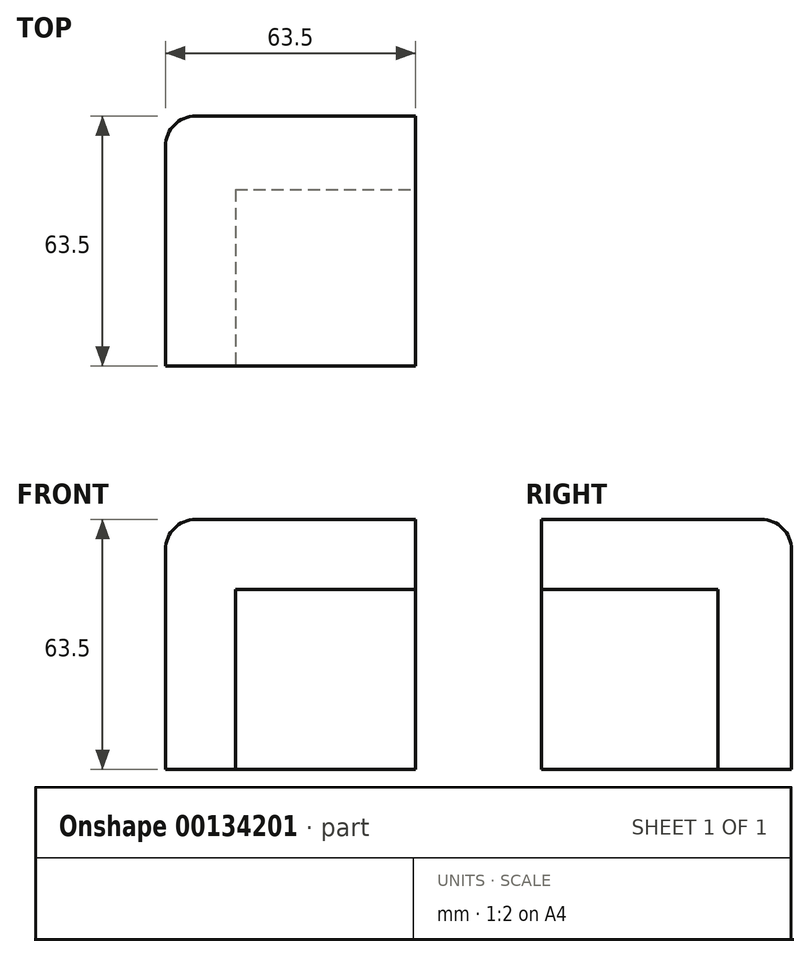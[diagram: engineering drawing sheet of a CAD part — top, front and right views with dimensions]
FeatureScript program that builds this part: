
annotation { "Feature Type Name" : "Feature", "Feature Type Description" : "" }
export const myFeature = defineFeature(function(context is Context, id is Id, definition is map)
    precondition{}
    {
        {
            var Q0;
            Q0=qCreatedBy(makeId("Front.planeOp"),FACE);
            var sketch = newSketch(context, id + "F0", { "sketchPlane" : qUnion([Q0])});
            skLineSegment(sketch, "E0.bottom", {"start": v(-31.75, 31.75) * mm, "end": v(31.75, 31.75) * mm});
            skLineSegment(sketch, "E0.top", {"start": v(-31.75, -31.75) * mm, "end": v(31.75, -31.75) * mm});
            skLineSegment(sketch, "E0.left", {"start": v(-31.75, 31.75) * mm, "end": v(-31.75, -31.75) * mm});
            skLineSegment(sketch, "E0.right", {"start": v(31.75, 31.75) * mm, "end": v(31.75, -31.75) * mm});
            skPoint(sketch, "E0.middle", {"position": v(0, 0) * mm});
            skSolve(sketch);
        }
        {
            var Q0;
            Q0=makeQuery(id+"F0.imprint","IMPRINT",FACE,{"disambiguationData":[TD([[makeQuery(id+"F0.imprint","IMPRINT",EDGE,{"derivedFrom":sQuery(id+"F0.wireOp",EDGE,"E0.bottom")}),-1.0]])]});
            extrude(context, id + "F1", {"entities" : qUnion([Q0]), "depth" : 63.5 * mm});
        }
        {
            var Q0;
            Q0=makeQuery(id+"F1.opExtrude","CAP_FACE",FACE,{"disambiguationData":[OSD([sQuery(id+"F0.wireOp",EDGE,"E0.bottom"),sQuery(id+"F0.wireOp",EDGE,"E0.top"),sQuery(id+"F0.wireOp",EDGE,"E0.left"),sQuery(id+"F0.wireOp",EDGE,"E0.right")])],"isStart":false});
            var sketch = newSketch(context, id + "F2", { "sketchPlane" : qUnion([Q0])});
            skLineSegment(sketch, "E1.bottom", {"start": v(31.75, -31.75) * mm, "end": v(-13.97, -31.75) * mm});
            skLineSegment(sketch, "E1.top", {"start": v(31.75, 13.97) * mm, "end": v(-13.97, 13.97) * mm});
            skLineSegment(sketch, "E1.left", {"start": v(31.75, -31.75) * mm, "end": v(31.75, 13.97) * mm});
            skLineSegment(sketch, "E1.right", {"start": v(-13.97, -31.75) * mm, "end": v(-13.97, 13.97) * mm});
            skSolve(sketch);
        }
        {
            var Q0;
            Q0=makeQuery(id+"F2.imprint","IMPRINT",FACE,{"disambiguationData":[TD([[makeQuery(id+"F2.imprint","IMPRINT",EDGE,{"derivedFrom":sQuery(id+"F2.wireOp",EDGE,"E1.bottom")}),1.0]])]});
            extrude(context, id + "F3", {"entities" : qUnion([Q0]), "operationType" : NewBodyOperationType.REMOVE, "oppositeDirection" : true, "depth" : 44.77 * mm});
        }
        {
            var Q0;
            Q0=makeQuery(id+"F1.opExtrude","CAP_EDGE",EDGE,{"disambiguationData":[OSD([sQuery(id+"F0.wireOp",EDGE,"E0.left")])],"isStart":true});
            var Q1;
            Q1=makeQuery(id+"F1.opExtrude","SWEPT_EDGE",EDGE,{"disambiguationData":[OSD([sQuery(id+"F0.wireOp",EDGE,"E0.bottom"),sQuery(id+"F0.wireOp",EDGE,"E0.left")])]});
            var Q2;
            Q2=makeQuery(id+"F1.opExtrude","CAP_EDGE",EDGE,{"disambiguationData":[OSD([sQuery(id+"F0.wireOp",EDGE,"E0.bottom")])],"isStart":true});
            fillet(context, id + "F4", {"entities" : qUnion([Q0, Q1, Q2]), "radius" : 7.62 * mm, "tangentPropagation" : true, "allowEdgeOverflow" : false});
        }
    });
